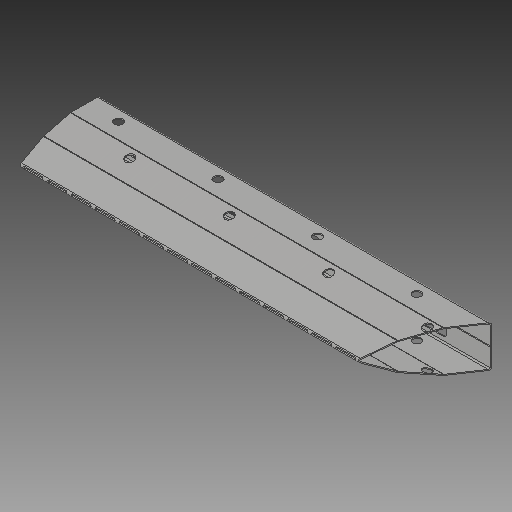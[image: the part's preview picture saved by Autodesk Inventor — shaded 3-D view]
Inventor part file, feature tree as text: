
AUTODESK INVENTOR PART (.ipt)
format: ipt  version: 2018 (Build 220112000, 112)  size: 860,672 bytes
history: native  units: mm
features: reference x24, other x23, sketch x16, sheet_metal_op x13, plane x9, projected_geometry x8, extrude x6
ambient origin geometry x8: Origin, YZ Plane, XZ Plane, XY Plane, X Axis, Y Axis, Z Axis, Center Point
bodies: Solid1 (feature_tree)
feature tree (99):
  parser-record x4  (decoder bookkeeping rows leaked as tree rows — omitted from the tree; the rows remain in map.json)
  plane  "Work Plane1"
  sheet_metal_op  "Face1"
  plane  "Work Plane2"
  sheet_metal_op  "Face2"
  plane  "Work Plane3"
  sheet_metal_op  "Face3"
  plane  "Work Plane4"
  sheet_metal_op  "Face4"
  plane  "Work Plane5"
  sheet_metal_op  "Face5"
  plane  "Work Plane6"
  sheet_metal_op  "Face6"
  plane  "Work Plane7"
  sheet_metal_op  "Face7"
  other  "midtplan"
  extrude  "afskær bund"  Depth=3.75mm
  extrude  "afskær top"  Depth=1.5mm
  extrude  "hulsæt til stifter"  Depth=3.75mm
  sketch  "Sketch14"  dims[d16=3.75mm]
  plane  "Work Plane12"
  extrude  "balusterhul"  Depth=3.0mm
  extrude  "balusterhul skråkompensering"  Depth=6.0mm
  extrude  "test"  Depth=3.75mm
  sketch  "Sketch1"  dims[d0=3.0mm d1=3.75mm]
  reference  "Reference1"
  reference  "Reference2"
  reference  "Reference3"
  reference  "Reference4"
  other  "Plate1"
  sketch  "Sketch2"  dims[d2=3.0mm d3=1.5mm]
  reference  "Reference5"
  reference  "Reference6"
  reference  "Reference7"
  reference  "Reference8"
  other  "Plate2"
  sheet_metal_op  "Bend1"
  sketch  "Sketch3"  dims[d4=6.0mm d5=3.75mm]
  reference  "Reference9"
  reference  "Reference10"
  reference  "Reference11"
  other  "Plate3"
  sheet_metal_op  "Bend2"
  sketch  "Sketch4"  dims[d6=3.75mm d7=3.0mm]
  reference  "Reference12"
  reference  "Reference13"
  reference  "Reference14"
  reference  "Reference15"
  other  "Plate4"
  sheet_metal_op  "Bend3"
  sketch  "Sketch5"  dims[d8=1.5mm d9=6.0mm]
  reference  "Reference16"
  reference  "Reference17"
  reference  "Reference18"
  other  "Plate5"
  sheet_metal_op  "Bend4"
  sketch  "Sketch6"  dims[d10=3.75mm d11=3.75mm]
  reference  "Reference19"
  reference  "Reference20"
  reference  "Reference21"
  other  "Plate6"
  sheet_metal_op  "Bend5"
  sketch  "Sketch7"  dims[d12=3.0mm]
  reference  "Reference22"
  reference  "Reference23"
  other  "Plate7"
  sheet_metal_op  "Bend6"
  sketch  "Sketch8"  dims[d13=1.5mm]
  reference  "Reference24"
  projected_geometry  "Projected Loop1"
  other  "huller til stifter"
  projected_geometry  "Projected Loop3"
  sketch  "Sketch12"  dims[d14=6.0mm]
  projected_geometry  "Projected Loop4"
  sketch  "Sketch13"  dims[d15=3.75mm]
  projected_geometry  "Projected Loop5"
  plane  "Work Plane11"
  sketch  "Sketch15"  dims[d17=3.0mm]
  sketch  "Sketch16"  dims[d18=1.5mm]
  projected_geometry  "Projected Loop6"
  projected_geometry  "Projected Loop7"
  sketch  "Sketch17"  dims[d19=6.0mm]
  projected_geometry  "Projected Loop8"
  projected_geometry  "Projected Loop9"
  sketch  "Sketch18"  dims[d20=3.75mm]
  sketch  "Sketch20"  dims[d21=3.75mm d22=3.0mm d23=1.5mm d24=6.0mm d25=3.75mm d26=3.75mm d27=3.0mm d28=1.5mm d29=6.0mm d30=3.75mm d31=3.0mm d32=0.0mm d33=3.0mm d39=250.0mm d41=33.7mm d42=33.7mm d43=60.0mm d44=70.0mm d45=16.85mm d46=65.0mm d47=60.0mm d48=10.0mm d49=0.0mm d50=250.0mm d51=33.7mm d52=33.7mm d53=60.0mm d54=16.85mm d55=65.0mm d56=60.0mm d57=30.0mm d59=302.736671mm d60=10.0mm d62=10.0mm d65=302.736671mm d66=195.343893mm d68=306.228mm d69=10.0mm d70=0.0mm d71=96.671937mm d74=10.0mm d75=0.0mm d76=5.986479mm d77=26.6mm d78=25.8mm d79=26.6mm d80=26.6mm d81=26.6mm d82=26.6mm d83=26.6mm d84=26.6mm d85=39.001254mm d95=113.170852mm d96=56.585426mm d97=90.0deg d98=49.5mm d99=100.0mm d100=0.0mm d101=2.046461mm d102=1.023231mm d103=10.0mm d104=0.0mm d105=90.0mm d106=342.765mm d107=342.765mm d108=30.0mm d109=30.0mm d110=30.0mm d111=342.765mm d112=10.0mm d113=3.0mm d114=0.0mm d115=6.0mm d116=61.0mm d117=8.0mm d118=150.0mm d120=73.2mm d121=10.0mm d123=10.0mm d125=3.0mm d126=0.0mm d129=10.0mm d130=0.0mm d131=1.0mm d132=1.0mm d133=1.0mm d134=1.0mm d135=140.0mm]
  other  "Cut1"
  other  "plantehuller"
  other  "bukkeperforering"
  other  "modul top.iam"
  other  "model:1"
  other  "Definition1"
  other  "modul.iam"
  other  "søjle+vange.iam"
  other  "stilladssøjle:2"
  other  "rør:1"
note: 4 file-system paths scrubbed to <path> (originals preserved in map.json)
